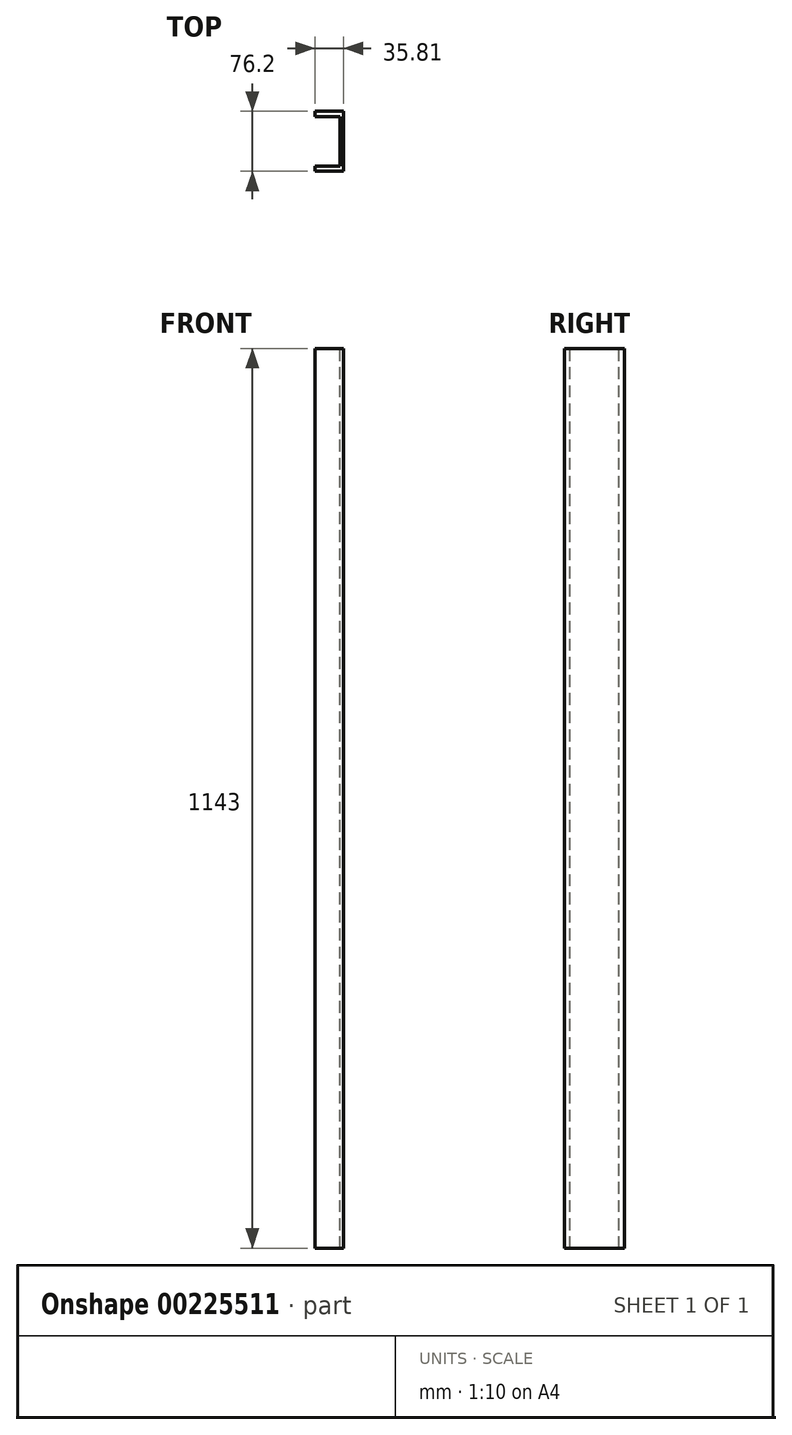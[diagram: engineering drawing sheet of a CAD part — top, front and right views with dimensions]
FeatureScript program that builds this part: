
annotation { "Feature Type Name" : "Feature", "Feature Type Description" : "" }
export const myFeature = defineFeature(function(context is Context, id is Id, definition is map)
    precondition{}
    {
        {
            var Q0;
            Q0=qCreatedBy(makeId("Right.planeOp"),FACE);
            var sketch = newSketch(context, id + "F0", { "sketchPlane" : qUnion([Q0])});
            skLineSegment(sketch, "E0.bottom", {"start": v(-76.2, 1354.6) * mm, "end": v(0, 1354.6) * mm});
            skLineSegment(sketch, "E0.top", {"start": v(-76.2, 211.6) * mm, "end": v(0, 211.6) * mm});
            skLineSegment(sketch, "E0.left", {"start": v(-76.2, 1354.6) * mm, "end": v(-76.2, 211.6) * mm});
            skLineSegment(sketch, "E0.right", {"start": v(0, 1354.6) * mm, "end": v(0, 211.6) * mm});
            skSolve(sketch);
        }
        {
            var Q0;
            Q0 = qSketchRegion(id + "F0", true);
            extrude(context, id + "F1", {"entities" : qUnion([Q0]), "oppositeDirection" : true, "depth" : 35.81 * mm});
        }
        {
            var Q0;
            Q0=makeQuery(id+"F1.opExtrude","SWEPT_FACE",FACE,{"disambiguationData":[OSD([sQuery(id+"F0.wireOp",EDGE,"E0.bottom")])]});
            var sketch = newSketch(context, id + "F2", { "sketchPlane" : qUnion([Q0])});
            skLineSegment(sketch, "E1.bottom", {"start": v(-35.81, -69.27) * mm, "end": v(-4.32, -69.27) * mm});
            skLineSegment(sketch, "E1.top", {"start": v(-35.81, -6.93) * mm, "end": v(-4.32, -6.93) * mm});
            skLineSegment(sketch, "E1.left", {"start": v(-35.81, -69.27) * mm, "end": v(-35.81, -6.93) * mm});
            skLineSegment(sketch, "E1.right", {"start": v(-4.32, -69.27) * mm, "end": v(-4.32, -6.93) * mm});
            skSolve(sketch);
        }
        {
            var Q0;
            Q0 = qSketchRegion(id + "F2", true);
            extrude(context, id + "F3", {"entities" : qUnion([Q0]), "operationType" : NewBodyOperationType.REMOVE, "endBound" : BoundingType.THROUGH_ALL, "oppositeDirection" : true, "depth" : 25.4 * mm});
        }
    });
